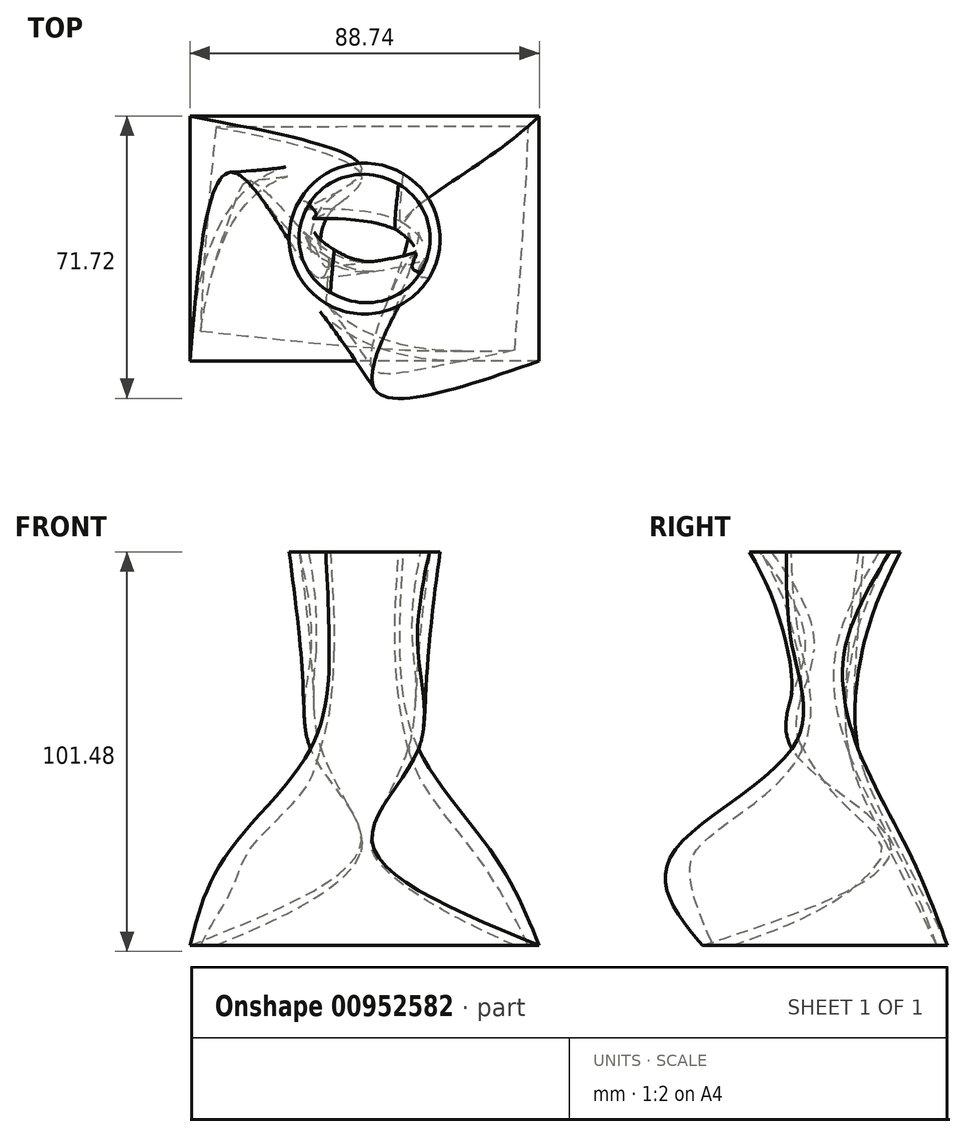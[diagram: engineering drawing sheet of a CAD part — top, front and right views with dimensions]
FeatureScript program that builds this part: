
annotation { "Feature Type Name" : "Feature", "Feature Type Description" : "" }
export const myFeature = defineFeature(function(context is Context, id is Id, definition is map)
    precondition{}
    {
        {
            var Q0;
            Q0=qCreatedBy(makeId("Top.planeOp"),FACE);
            var sketch = newSketch(context, id + "F0", { "sketchPlane" : qUnion([Q0])});
            skPoint(sketch, "E0.0.midPoint", {"position": v(-10.57, 12.32) * mm});
            skLineSegment(sketch, "E1.bottom", {"start": v(13.72, -8.42) * mm, "end": v(-13.72, -8.42) * mm});
            skLineSegment(sketch, "E1.top", {"start": v(13.72, 8.42) * mm, "end": v(-13.72, 8.42) * mm});
            skLineSegment(sketch, "E1.left", {"start": v(13.72, -8.42) * mm, "end": v(13.72, 8.42) * mm});
            skLineSegment(sketch, "E1.right", {"start": v(-13.72, -8.42) * mm, "end": v(-13.72, 8.42) * mm});
            skPoint(sketch, "E1.middle", {"position": v(0, 0) * mm});
            skSolve(sketch);
        }
        {
            var Q0;
            Q0=qCreatedBy(makeId("Top.planeOp"),FACE);
            cPlane(context, id + "F1", {"entities" : qUnion([Q0]), "cplaneType" : CPlaneType.OFFSET, "offset" : 25 * mm, "width" : 150 * mm, "height" : 150 * mm});
        }
        {
            var Q0;
            Q0=qCreatedBy(id+"F1.planeOp",FACE);
            var sketch = newSketch(context, id + "F2", { "sketchPlane" : qUnion([Q0])});
            skPoint(sketch, "E2.0.midPoint", {"position": v(11.93, 7.27) * mm});
            skPoint(sketch, "E3.0.midPoint", {"position": v(17.8, -9) * mm});
            skEllipse(sketch, "E4", {"center": v(0, 0) * mm, "majorRadius": 16.9 * mm, "minorRadius": 8.32 * mm, "majorAxis": v(0.95, -0.31)});
            skSolve(sketch);
        }
        {
            var Q0;
            Q0=qCreatedBy(id+"F1.planeOp",FACE);
            cPlane(context, id + "F3", {"entities" : qUnion([Q0]), "cplaneType" : CPlaneType.OFFSET, "offset" : 25 * mm, "width" : 150 * mm, "height" : 150 * mm});
        }
        {
            var Q0;
            Q0=qCreatedBy(id+"F3.planeOp",FACE);
            var sketch = newSketch(context, id + "F4", { "sketchPlane" : qUnion([Q0])});
            skPoint(sketch, "E5.middle", {"position": v(0, 0) * mm});
            skCircle(sketch, "E6", {"center": v(0, 0) * mm, "radius": 19.16 * mm});
            skSolve(sketch);
        }
        {
            var Q0;
            Q0=qCreatedBy(makeId("Top.planeOp"),FACE);
            cPlane(context, id + "F5", {"entities" : qUnion([Q0]), "cplaneType" : CPlaneType.OFFSET, "offset" : 25 * mm, "oppositeDirection" : true, "width" : 150 * mm, "height" : 150 * mm});
        }
        {
            var Q0;
            Q0=qCreatedBy(id+"F5.planeOp",FACE);
            var sketch = newSketch(context, id + "F6", { "sketchPlane" : qUnion([Q0])});
            skPoint(sketch, "E7.middle", {"position": v(0, 0) * mm});
            skCircle(sketch, "E8.cCircle", {"center": v(0, 0) * mm, "radius": 18.82 * mm, "construction": true});
            skLineSegment(sketch, "E8.0", {"start": v(31.41, 20.72) * mm, "end": v(2.24, -37.56) * mm});
            skLineSegment(sketch, "E8.1", {"start": v(2.24, -37.56) * mm, "end": v(-33.65, 16.84) * mm});
            skLineSegment(sketch, "E8.2", {"start": v(-33.65, 16.84) * mm, "end": v(31.41, 20.72) * mm});
            skPoint(sketch, "E8.0.midPoint", {"position": v(16.83, -8.42) * mm});
            skSolve(sketch);
        }
        {
            var Q0;
            Q0=qCreatedBy(id+"F5.planeOp",FACE);
            cPlane(context, id + "F7", {"entities" : qUnion([Q0]), "cplaneType" : CPlaneType.OFFSET, "offset" : 25 * mm, "oppositeDirection" : true, "width" : 150 * mm, "height" : 150 * mm});
        }
        {
            var Q0;
            Q0=qCreatedBy(id+"F7.planeOp",FACE);
            var sketch = newSketch(context, id + "F8", { "sketchPlane" : qUnion([Q0])});
            skPoint(sketch, "E9.middle", {"position": v(0, 0) * mm});
            skLineSegment(sketch, "E10.bottom", {"start": v(44.37, -31.12) * mm, "end": v(-44.37, -31.12) * mm});
            skLineSegment(sketch, "E10.top", {"start": v(44.37, 31.12) * mm, "end": v(-44.37, 31.12) * mm});
            skLineSegment(sketch, "E10.left", {"start": v(44.37, -31.12) * mm, "end": v(44.37, 31.12) * mm});
            skLineSegment(sketch, "E10.right", {"start": v(-44.37, -31.12) * mm, "end": v(-44.37, 31.12) * mm});
            skSolve(sketch);
        }
        {
            var Q0;
            Q0=makeQuery(id+"F8.imprint","IMPRINT",FACE,{"disambiguationData":[TD([[makeQuery(id+"F8.imprint","IMPRINT",EDGE,{"derivedFrom":sQuery(id+"F8.wireOp",EDGE,"E10.bottom")}),-1.0]])]});
            var Q1;
            Q1=makeQuery(id+"F6.imprint","IMPRINT",FACE,{"disambiguationData":[TD([[makeQuery(id+"F6.imprint","IMPRINT",EDGE,{"derivedFrom":sQuery(id+"F6.wireOp",EDGE,"E8.0")}),-1.0]])]});
            var Q2;
            Q2=makeQuery(id+"F0.imprint","IMPRINT",FACE,{"disambiguationData":[TD([[makeQuery(id+"F0.imprint","IMPRINT",EDGE,{"derivedFrom":sQuery(id+"F0.wireOp",EDGE,"E1.bottom")}),-1.0]])]});
            var Q3;
            Q3=makeQuery(id+"F2.imprint","IMPRINT",FACE,{"disambiguationData":[TD([[makeQuery(id+"F2.imprint","IMPRINT",EDGE,{"derivedFrom":sQuery(id+"F2.wireOp",EDGE,"E4")}),1.0]])]});
            var Q4;
            Q4=makeQuery(id+"F4.imprint","IMPRINT",FACE,{"disambiguationData":[TD([[makeQuery(id+"F4.imprint","IMPRINT",EDGE,{"derivedFrom":sQuery(id+"F4.wireOp",EDGE,"E6")}),1.0]])]});
            loft(context, id + "F9", {"sheetProfilesArray" : [{ "sheetProfileEntities" : qUnion([Q0]) }, { "sheetProfileEntities" : qUnion([Q1]) }, { "sheetProfileEntities" : qUnion([Q2]) }, { "sheetProfileEntities" : qUnion([Q3]) }, { "sheetProfileEntities" : qUnion([Q4]) }]});
        }
        {
            var Q0;
            Q0=makeQuery(id+"F9.opLoft","CAP_FACE",FACE,{"disambiguationData":[OSD([makeQuery(id+"F4.imprint","IMPRINT",FACE,{"disambiguationData":[TD([[makeQuery(id+"F4.imprint","IMPRINT",EDGE,{"derivedFrom":sQuery(id+"F4.wireOp",EDGE,"E6")}),1.0]])]})])],"isStart":true});
            var Q1;
            Q1=makeQuery(id+"F9.opLoft","CAP_FACE",FACE,{"disambiguationData":[OSD([makeQuery(id+"F8.imprint","IMPRINT",FACE,{"disambiguationData":[TD([[makeQuery(id+"F8.imprint","IMPRINT",EDGE,{"derivedFrom":sQuery(id+"F8.wireOp",EDGE,"E10.bottom")}),-1.0]])]})])],"isStart":true});
            shell(context, id + "F10", {"entities" : qUnion([Q0, Q1]), "thickness" : 2.5 * mm});
        }
    });
